# Revit family: Hydrant_Post_Zurn-Z1390
name_source: partatom
category: Plumbing Fixtures
units: mm (PartAtom-declared; Revit-internal decimal feet)

## family parameters
Cut with Voids When Loaded = No
Host = Face
Maintain Annotation Orientation = No
OmniClass Number = 23.65.70.11.11
OmniClass Title = Fixtures for Liquids
Part Type = Normal
Room Calculation Point = No
Round Connector Dimension = Use Diameter
Shared = No

## types (5) — shared parameters
Assembly Code = D2020100
CW Connection = Yes
Default Elevation = 4' - 0"
Description = Post Hydrant Exposed Head, Non-Freeze
Female N.P.T. = 0' - 1 1/2"
HW Connection = No
Head = Bronze - Zurn - Cast
Hose Connection = 0' - 1 1/2"
Hydrant Casing = Steel - Zurn - Galvanized
Main Material = Steel - Zurn - Galvanized
Manufacturer = Zurn Water, LLC
Manufacturer Brand = Zurn
Model = Z1390
Modified Date = October 2, 2025
Parts List / Service Guide = https://files.zurn.com
Product Documentation Link = https://files.zurn.com
Product Page URL = https://www.zurn.com
Product data url = https://bimobject.com
URL = www.zurn.com
Valve Housing = Bronze - Zurn - Cast
Vent Connection = No
Waste Connection = No

## per-type parameters (varying)
| type | Approx Weight (Lbs) | Depth of Bury | Type Comments |
| Depth of Bury 4 Feet | 67 | 4' - 0" | Z1390-4 |
| Depth of Bury 3 Feet | 62 | 3' - 0" | Z1390-3 |
| Depth of Bury 5 Feet | 72 | 5' - 0" | Z1390-5 |
| Depth of Bury 6 Feet | 77 | 6' - 0" | Z1390-6 |
| Depth of Bury 8 Feet | 87 | 8' - 0" | Z1390-6 |

## geometry (parser evidence)
native form markers: Sweep x3
no freeform markers — native parametric forms only
